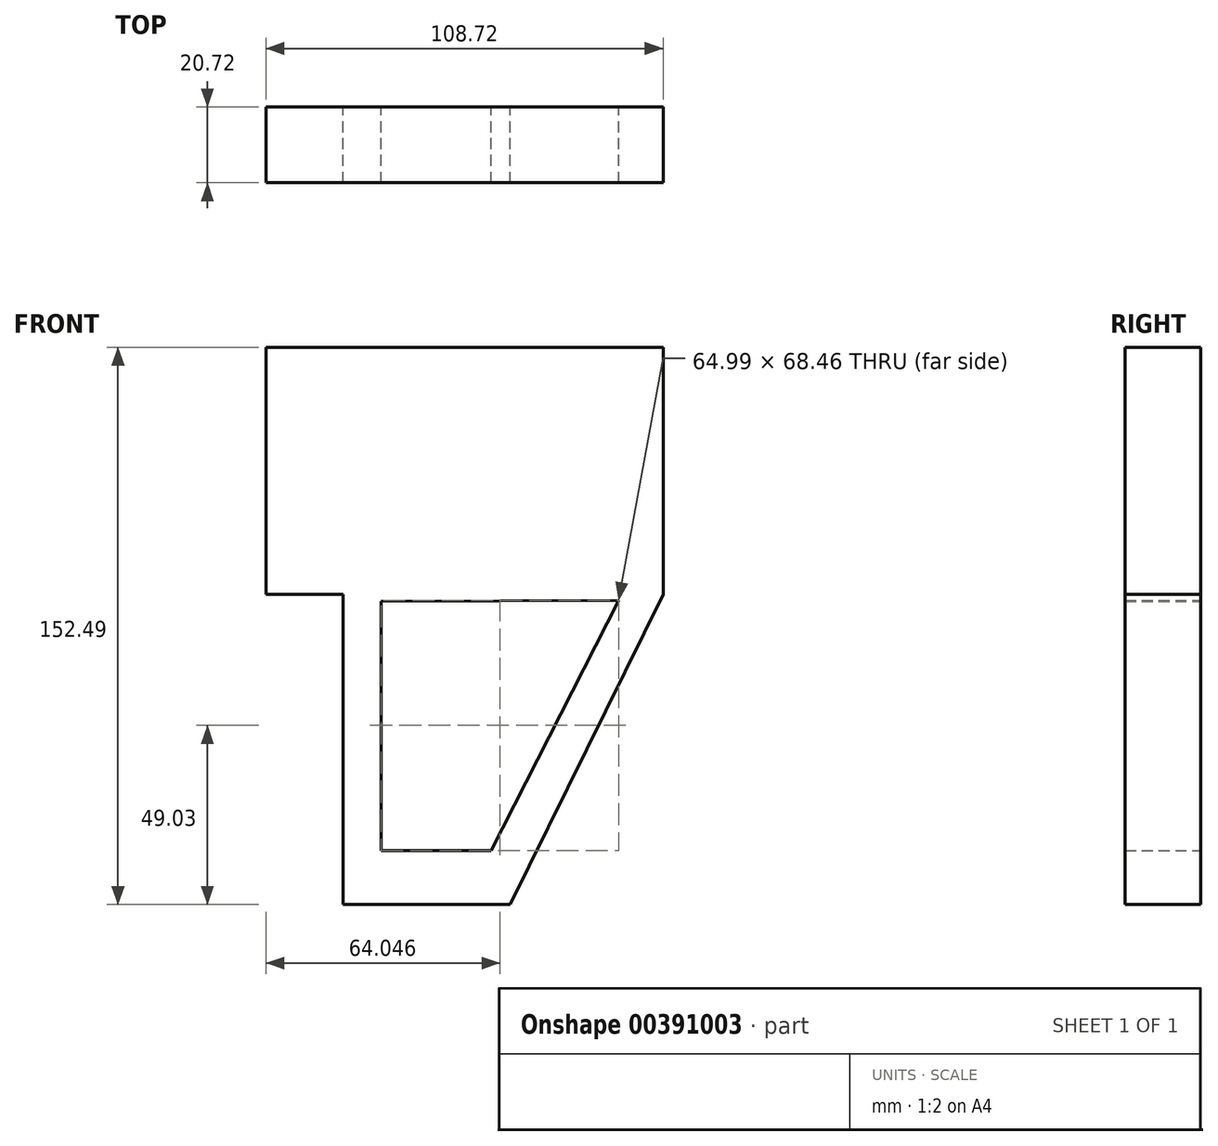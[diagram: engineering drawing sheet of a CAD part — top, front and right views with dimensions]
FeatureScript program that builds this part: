
annotation { "Feature Type Name" : "Feature", "Feature Type Description" : "" }
export const myFeature = defineFeature(function(context is Context, id is Id, definition is map)
    precondition{}
    {
        {
            var Q0;
            Q0=qCreatedBy(makeId("Front.planeOp"),FACE);
            var sketch = newSketch(context, id + "F0", { "sketchPlane" : qUnion([Q0])});
            skLineSegment(sketch, "E0.bottom", {"start": v(54.36, 33.82) * mm, "end": v(-54.36, 33.82) * mm});
            skLineSegment(sketch, "E0.top", {"start": v(54.36, -33.82) * mm, "end": v(-54.36, -33.82) * mm});
            skLineSegment(sketch, "E0.left", {"start": v(54.36, 33.82) * mm, "end": v(54.36, -33.82) * mm});
            skLineSegment(sketch, "E0.right", {"start": v(-54.36, 33.82) * mm, "end": v(-54.36, -33.82) * mm});
            skPoint(sketch, "E0.middle", {"position": v(0, 0) * mm});
            skLineSegment(sketch, "E1", {"start": v(54.36, -33.82) * mm, "end": v(12.48, -118.67) * mm});
            skLineSegment(sketch, "E2", {"start": v(12.48, -118.67) * mm, "end": v(-33.27, -118.67) * mm});
            skLineSegment(sketch, "E3", {"start": v(-33.27, -118.67) * mm, "end": v(-33.27, -33.82) * mm});
            skSolve(sketch);
        }
        {
            var Q0;
            Q0 = qSketchRegion(id + "F0", true);
            extrude(context, id + "F1", {"entities" : qUnion([Q0]), "depth" : 20.72 * mm});
        }
        {
            var Q0;
            Q0=qCreatedBy(makeId("Front.planeOp"),FACE);
            var sketch = newSketch(context, id + "F2", { "sketchPlane" : qUnion([Q0])});
            skLineSegment(sketch, "E4", {"start": v(-22.81, -35.7) * mm, "end": v(-22.81, -103.87) * mm});
            skLineSegment(sketch, "E5", {"start": v(-22.81, -103.87) * mm, "end": v(7.23, -103.87) * mm});
            skLineSegment(sketch, "E6", {"start": v(7.23, -103.87) * mm, "end": v(42.18, -35.4) * mm});
            skLineSegment(sketch, "E7", {"start": v(42.18, -35.4) * mm, "end": v(-22.81, -35.7) * mm});
            skSolve(sketch);
        }
        {
            var Q0;
            Q0 = qSketchRegion(id + "F2", true);
            extrude(context, id + "F3", {"entities" : qUnion([Q0]), "operationType" : NewBodyOperationType.REMOVE, "depth" : 25.4 * mm});
        }
    });
